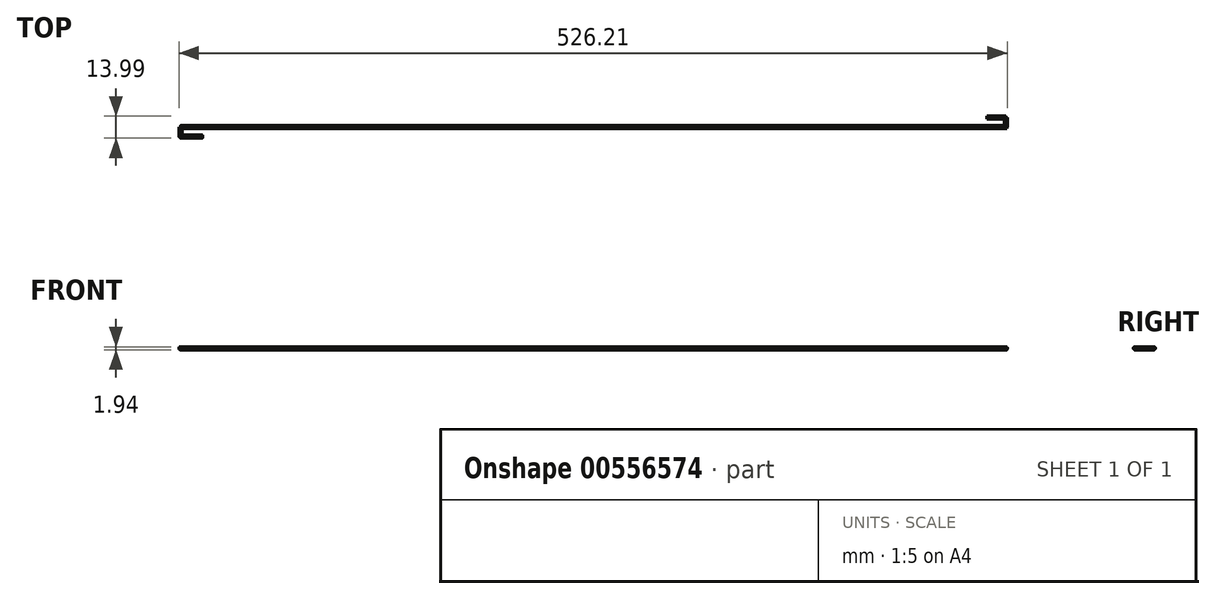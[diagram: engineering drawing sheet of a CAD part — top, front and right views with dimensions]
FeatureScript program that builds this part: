
annotation { "Feature Type Name" : "Feature", "Feature Type Description" : "" }
export const myFeature = defineFeature(function(context is Context, id is Id, definition is map)
    precondition{}
    {
        {
            var Q0;
            Q0=qCreatedBy(makeId("Right.planeOp"),FACE);
            var sketch = newSketch(context, id + "F0", { "sketchPlane" : qUnion([Q0])});
            skCircle(sketch, "E0", {"center": v(0, 0) * mm, "radius": 0.97 * mm});
            skSolve(sketch);
        }
        {
            var Q0;
            Q0 = qSketchRegion(id + "F0", true);
            extrude(context, id + "F1", {"entities" : qUnion([Q0]), "depth" : 525 * mm, "offsetDistance" : 25 * mm});
        }
        {
            var Q0;
            Q0=qCreatedBy(makeId("Front.planeOp"),FACE);
            var sketch = newSketch(context, id + "F2", { "sketchPlane" : qUnion([Q0])});
            skCircle(sketch, "E1", {"center": v(0, 0) * mm, "radius": 0.97 * mm});
            skSolve(sketch);
        }
        {
            var Q0;
            Q0 = qSketchRegion(id + "F2", true);
            extrude(context, id + "F3", {"entities" : qUnion([Q0]), "operationType" : NewBodyOperationType.ADD, "depth" : 6 * mm, "offsetDistance" : 25 * mm});
        }
        {
            var Q0;
            Q0=qCreatedBy(makeId("Right.planeOp"),FACE);
            var sketch = newSketch(context, id + "F4", { "sketchPlane" : qUnion([Q0])});
            skCircle(sketch, "E2", {"center": v(-4.02, 0) * mm, "radius": 0.97 * mm});
            skSolve(sketch);
        }
        {
            var Q0;
            Q0=makeQuery(id+"F1.opExtrude","SWEPT_BODY",BODY,{"disambiguationData":[OSD([sQuery(id+"F0.wireOp",EDGE,"E0")])]});
            transform(context, id + "F5", {"entities" : qUnion([Q0]), "transformType" : TransformType.TRANSLATION_3D, "dx" : 0 * mm, "dy" : 2 * mm, "dz" : 0 * mm, "makeCopy" : false});
        }
        {
            var Q0;
            Q0 = qSketchRegion(id + "F4", true);
            extrude(context, id + "F6", {"entities" : qUnion([Q0]), "operationType" : NewBodyOperationType.ADD, "depth" : 14 * mm, "offsetDistance" : 25 * mm});
        }
        {
            var Q0;
            Q0=qCreatedBy(makeId("Front.planeOp"),FACE);
            var sketch = newSketch(context, id + "F7", { "sketchPlane" : qUnion([Q0])});
            skCircle(sketch, "E3", {"center": v(524.27, 0) * mm, "radius": 0.97 * mm});
            skSolve(sketch);
        }
        {
            var Q0;
            Q0=makeQuery(id+"F7.imprint","IMPRINT",FACE,{"disambiguationData":[TD([[makeQuery(id+"F7.imprint","IMPRINT",EDGE,{"derivedFrom":sQuery(id+"F7.wireOp",EDGE,"E3")}),1.0]])]});
            extrude(context, id + "F8", {"entities" : qUnion([Q0]), "depth" : 6 * mm, "offsetDistance" : 25 * mm});
        }
        {
            var Q0;
            Q0=makeQuery(id+"F8.opExtrude","SWEPT_BODY",BODY,{"disambiguationData":[OSD([sQuery(id+"F7.wireOp",EDGE,"E3")])]});
            transform(context, id + "F9", {"entities" : qUnion([Q0]), "transformType" : TransformType.TRANSLATION_3D, "dx" : 0 * mm, "dy" : 8 * mm, "dz" : 0 * mm, "makeCopy" : false});
        }
        {
            var Q0;
            Q0=makeQuery(id+"F8.opExtrude","CAP_EDGE",EDGE,{"disambiguationData":[OSD([sQuery(id+"F7.wireOp",EDGE,"E3")])],"isStart":true});
            cPlane(context, id + "F10", {"entities" : qUnion([Q0]), "cplaneType" : CPlaneType.LINE_ANGLE, "offset" : 25 * mm, "angle" : 90 * degree, "width" : 150 * mm, "height" : 150 * mm});
        }
        {
            var Q0;
            Q0=qCreatedBy(id+"F10.planeOp",FACE);
            var sketch = newSketch(context, id + "F11", { "sketchPlane" : qUnion([Q0])});
            skCircle(sketch, "E4", {"center": v(8.03, 0) * mm, "radius": 0.97 * mm});
            skSolve(sketch);
        }
        {
            var Q0;
            Q0 = qSketchRegion(id + "F11", true);
            extrude(context, id + "F12", {"entities" : qUnion([Q0]), "operationType" : NewBodyOperationType.ADD, "depth" : -12 * mm, "offsetDistance" : 25 * mm});
        }
    });
